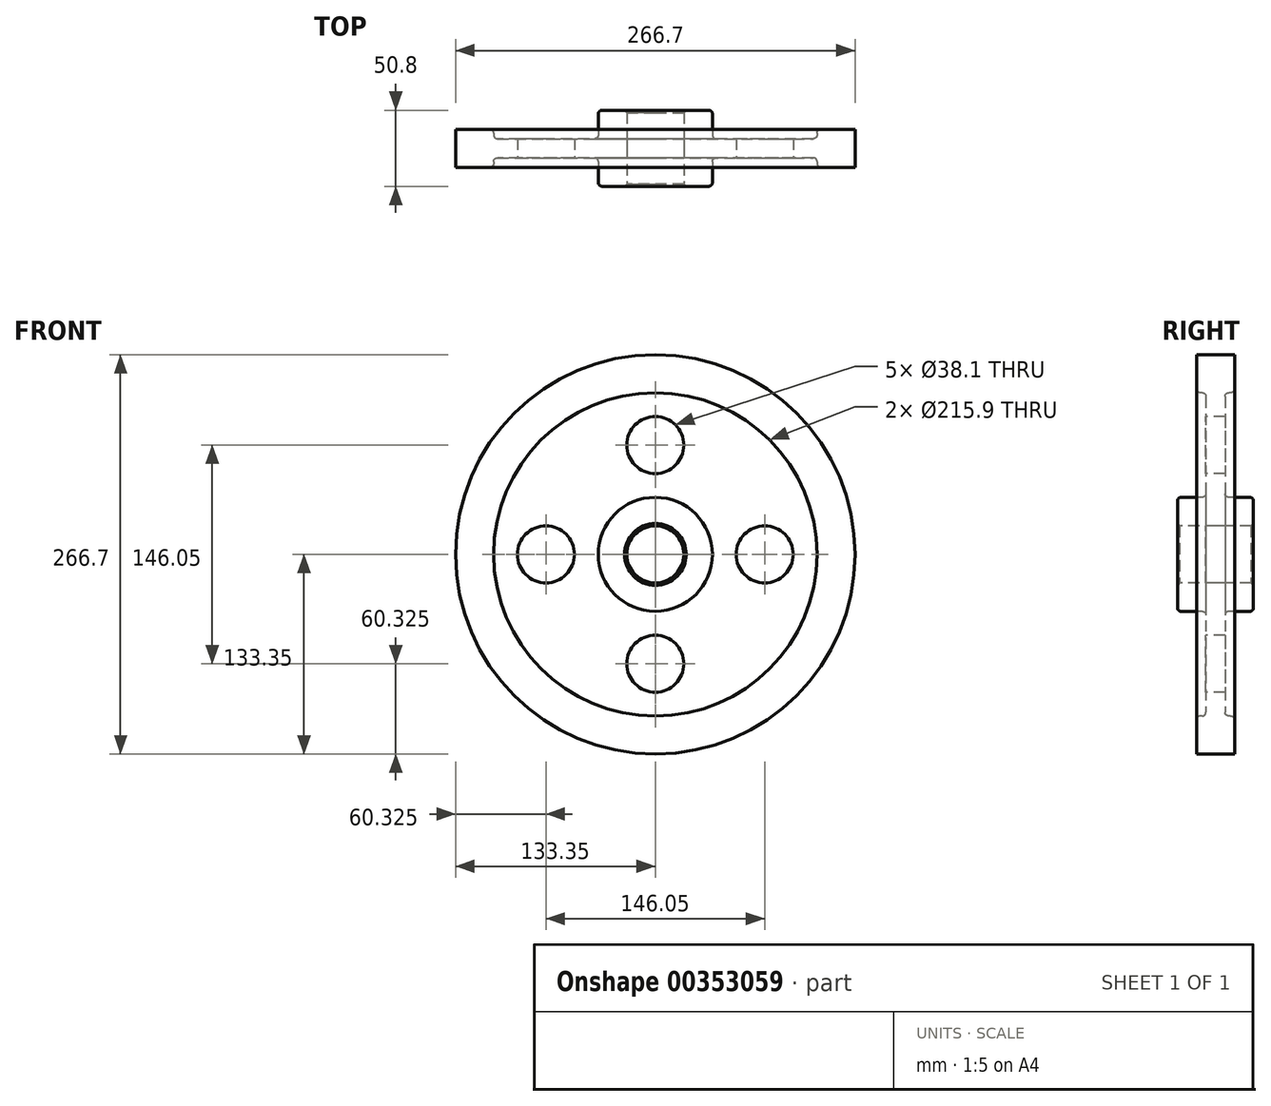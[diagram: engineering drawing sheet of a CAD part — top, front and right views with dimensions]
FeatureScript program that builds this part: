
annotation { "Feature Type Name" : "Feature", "Feature Type Description" : "" }
export const myFeature = defineFeature(function(context is Context, id is Id, definition is map)
    precondition{}
    {
        {
            var Q0;
            Q0=qCreatedBy(makeId("Right.planeOp"),FACE);
            var sketch = newSketch(context, id + "F0", { "sketchPlane" : qUnion([Q0])});
            skLineSegment(sketch, "E0", {"start": v(0, 0) * mm, "end": v(76.2, 0) * mm, "construction": true});
            skLineSegment(sketch, "E1.0", {"start": v(0, 19.05) * mm, "end": v(25.4, 19.05) * mm});
            skLineSegment(sketch, "E2.0", {"start": v(6.35, 38.1) * mm, "end": v(25.4, 38.1) * mm});
            skLineSegment(sketch, "E3.0", {"start": v(6.35, 107.95) * mm, "end": v(12.7, 107.95) * mm});
            skLineSegment(sketch, "E4.0", {"start": v(0, 133.35) * mm, "end": v(12.7, 133.35) * mm});
            skLineSegment(sketch, "E5.0", {"start": v(25.4, 38.1) * mm, "end": v(25.4, 19.05) * mm});
            skLineSegment(sketch, "E6.0", {"start": v(6.35, 107.95) * mm, "end": v(6.35, 38.1) * mm});
            skLineSegment(sketch, "E7", {"start": v(0, 133.35) * mm, "end": v(0, 19.05) * mm, "construction": true});
            skLineSegment(sketch, "E8.0", {"start": v(12.7, 133.35) * mm, "end": v(12.7, 107.95) * mm});
            skLineSegment(sketch, "E9.MirrorCS", {"start": v(-6.35, 107.95) * mm, "end": v(-6.35, 38.1) * mm});
            skLineSegment(sketch, "E10.MirrorCS", {"start": v(-6.35, 107.95) * mm, "end": v(-12.7, 107.95) * mm});
            skLineSegment(sketch, "E11.MirrorCS", {"start": v(-12.7, 133.35) * mm, "end": v(-12.7, 107.95) * mm});
            skLineSegment(sketch, "E12.MirrorCS", {"start": v(0, 133.35) * mm, "end": v(-12.7, 133.35) * mm});
            skLineSegment(sketch, "E13.MirrorCS", {"start": v(-6.35, 38.1) * mm, "end": v(-25.4, 38.1) * mm});
            skLineSegment(sketch, "E14.MirrorCS", {"start": v(-25.4, 38.1) * mm, "end": v(-25.4, 19.05) * mm});
            skLineSegment(sketch, "E15.MirrorCS", {"start": v(0, 19.05) * mm, "end": v(-25.4, 19.05) * mm});
            skSolve(sketch);
        }
        {
            var Q0;
            Q0=makeQuery(id+"F0.imprint","IMPRINT",FACE,{"disambiguationData":[TD([[makeQuery(id+"F0.imprint","IMPRINT",EDGE,{"derivedFrom":sQuery(id+"F0.wireOp",EDGE,"E1.0")}),1.0]])]});
            var Q1;
            Q1=sQuery(id+"F0.wireOp",EDGE,"E0");
            revolve(context, id + "F1", {"entities" : qUnion([Q0]), "axis" : qUnion([Q1]), "revolveType" : RevolveType.FULL});
        }
        {
            var Q0;
            Q0=makeQuery(id+"F1.opRevolve","SWEPT_FACE",FACE,{"disambiguationData":[OSD([sQuery(id+"F0.wireOp",EDGE,"E9.MirrorCS")])]});
            var sketch = newSketch(context, id + "F2", { "sketchPlane" : qUnion([Q0])});
            skLineSegment(sketch, "E16", {"start": v(0, 0) * mm, "end": v(0, 73.03) * mm});
            skCircle(sketch, "E17", {"center": v(0, 73.03) * mm, "radius": 19.05 * mm});
            skCircle(sketch, "E18.1.0", {"center": v(73.03, 0) * mm, "radius": 19.05 * mm});
            skCircle(sketch, "E18.2.0", {"center": v(0, -73.03) * mm, "radius": 19.05 * mm});
            skCircle(sketch, "E18.3.0", {"center": v(-73.03, 0) * mm, "radius": 19.05 * mm});
            skPoint(sketch, "E18.center", {"position": v(0, 0) * mm});
            skLineSegment(sketch, "E18.anchor1", {"start": v(0, 0) * mm, "end": v(0, 73.03) * mm, "construction": true});
            skLineSegment(sketch, "E18.anchor2", {"start": v(0, 0) * mm, "end": v(-73.03, 0) * mm, "construction": true});
            skSolve(sketch);
        }
        {
            var Q0;
            Q0=makeQuery(id+"F2.imprint","IMPRINT",FACE,{"disambiguationData":[TD([[makeQuery(id+"F2.imprint","IMPRINT",EDGE,{"derivedFrom":sQuery(id+"F2.wireOp",EDGE,"E18.3.0")}),1.0]])]});
            var Q1;
            Q1=makeQuery(id+"F2.imprint","IMPRINT",FACE,{"disambiguationData":[TD([[makeQuery(id+"F2.imprint","IMPRINT",EDGE,{"derivedFrom":sQuery(id+"F2.wireOp",EDGE,"E18.2.0")}),1.0]])]});
            var Q2;
            Q2=makeQuery(id+"F2.imprint","IMPRINT",FACE,{"disambiguationData":[TD([[makeQuery(id+"F2.imprint","IMPRINT",EDGE,{"derivedFrom":sQuery(id+"F2.wireOp",EDGE,"E18.1.0")}),1.0]])]});
            var Q3;
            Q3=makeQuery(id+"F2.imprint","IMPRINT",FACE,{"disambiguationData":[TD([[makeQuery(id+"F2.imprint","IMPRINT",EDGE,{"derivedFrom":sQuery(id+"F2.wireOp",EDGE,"E17")}),1.0]])]});
            extrude(context, id + "F3", {"entities" : qUnion([Q0, Q1, Q2, Q3]), "operationType" : NewBodyOperationType.REMOVE, "oppositeDirection" : true, "depth" : 25.4 * mm});
        }
        {
            var Q0;
            Q0=makeQuery(id+"F1.opRevolve","SWEPT_EDGE",EDGE,{"disambiguationData":[OSD([sQuery(id+"F0.wireOp",EDGE,"E9.MirrorCS"),sQuery(id+"F0.wireOp",EDGE,"E13.MirrorCS")])]});
            var Q1;
            Q1=makeQuery(id+"F1.opRevolve","SWEPT_EDGE",EDGE,{"disambiguationData":[OSD([sQuery(id+"F0.wireOp",EDGE,"E13.MirrorCS"),sQuery(id+"F0.wireOp",EDGE,"E14.MirrorCS")])]});
            var Q2;
            Q2=makeQuery(id+"F1.opRevolve","SWEPT_EDGE",EDGE,{"disambiguationData":[OSD([sQuery(id+"F0.wireOp",EDGE,"E10.MirrorCS"),sQuery(id+"F0.wireOp",EDGE,"E11.MirrorCS")])]});
            var Q3;
            Q3=makeQuery(id+"F1.opRevolve","SWEPT_EDGE",EDGE,{"disambiguationData":[OSD([sQuery(id+"F0.wireOp",EDGE,"E9.MirrorCS"),sQuery(id+"F0.wireOp",EDGE,"E10.MirrorCS")])]});
            var Q4;
            Q4=makeQuery(id+"F1.opRevolve","SWEPT_EDGE",EDGE,{"disambiguationData":[OSD([sQuery(id+"F0.wireOp",EDGE,"E3.0"),sQuery(id+"F0.wireOp",EDGE,"E8.0")])]});
            var Q5;
            Q5=makeQuery(id+"F1.opRevolve","SWEPT_EDGE",EDGE,{"disambiguationData":[OSD([sQuery(id+"F0.wireOp",EDGE,"E3.0"),sQuery(id+"F0.wireOp",EDGE,"E6.0")])]});
            var Q6;
            Q6=makeQuery(id+"F1.opRevolve","SWEPT_EDGE",EDGE,{"disambiguationData":[OSD([sQuery(id+"F0.wireOp",EDGE,"E2.0"),sQuery(id+"F0.wireOp",EDGE,"E5.0")])]});
            var Q7;
            Q7=makeQuery(id+"F1.opRevolve","SWEPT_FACE",FACE,{"disambiguationData":[OSD([sQuery(id+"F0.wireOp",EDGE,"E2.0")])]});
            fillet(context, id + "F4", {"entities" : qUnion([Q0, Q1, Q2, Q3, Q4, Q5, Q6, Q7]), "radius" : 2.54 * mm, "tangentPropagation" : true, "allowEdgeOverflow" : false});
        }
        {
            var Q0;
            Q0=makeQuery(id+"F1.opRevolve","SWEPT_EDGE",EDGE,{"disambiguationData":[OSD([sQuery(id+"F0.wireOp",EDGE,"E1.0"),sQuery(id+"F0.wireOp",EDGE,"E5.0")])]});
            var Q1;
            Q1=makeQuery(id+"F1.opRevolve","SWEPT_FACE",FACE,{"disambiguationData":[OSD([sQuery(id+"F0.wireOp",EDGE,"E1.0"),sQuery(id+"F0.wireOp",EDGE,"E15.MirrorCS")])]});
            chamfer(context, id + "F5", {"entities" : qUnion([Q0, Q1]), "width" : 1.59 * mm, "tangentPropagation" : true});
        }
    });
